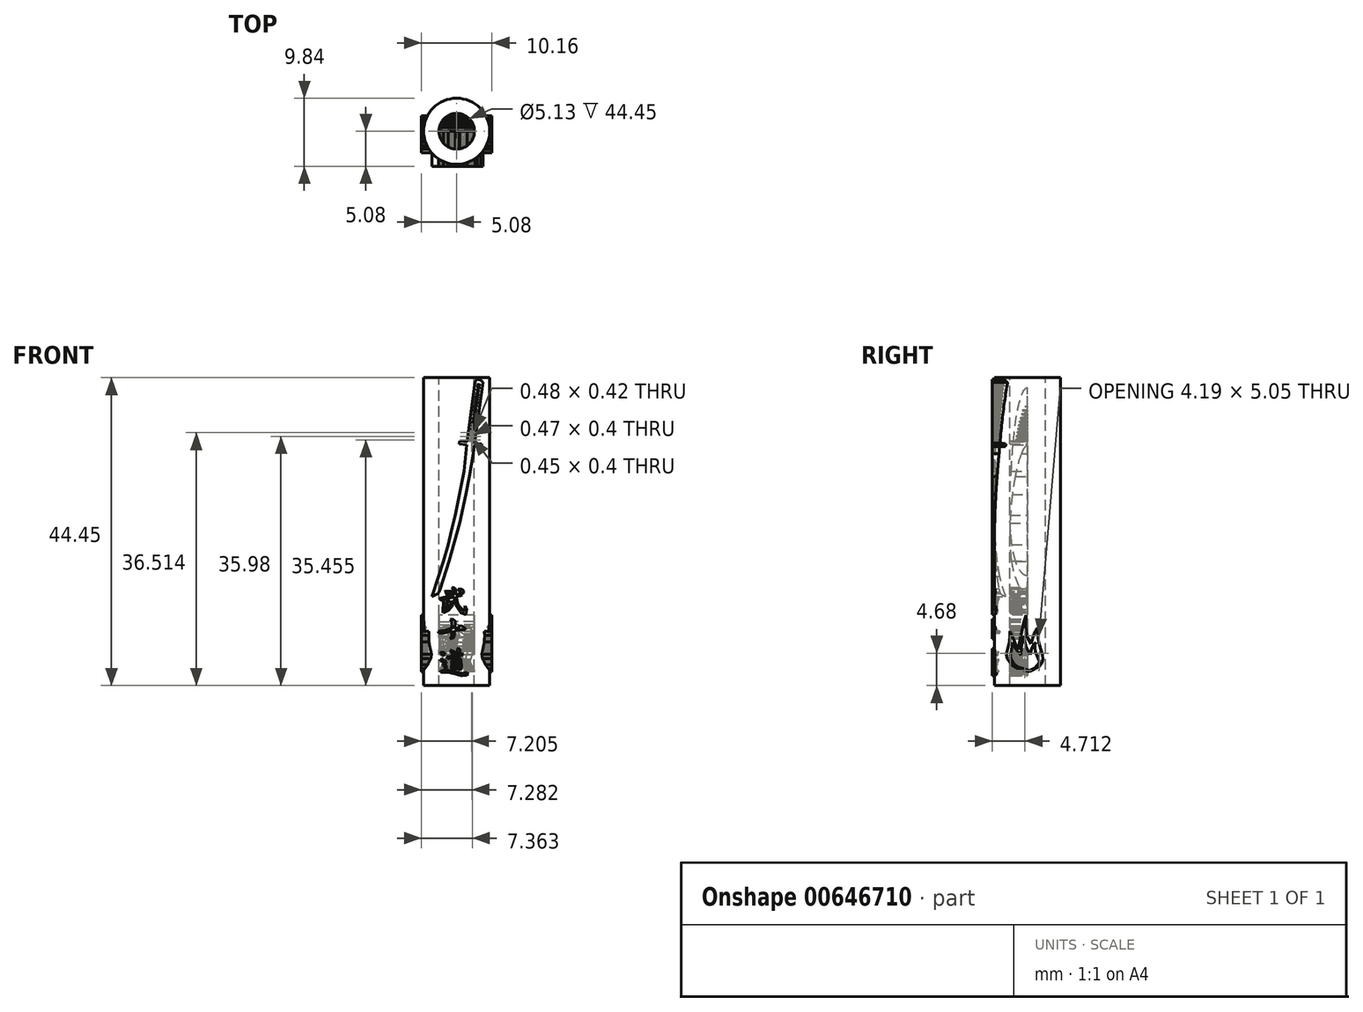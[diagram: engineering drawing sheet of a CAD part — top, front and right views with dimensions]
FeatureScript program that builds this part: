
annotation { "Feature Type Name" : "Feature", "Feature Type Description" : "" }
export const myFeature = defineFeature(function(context is Context, id is Id, definition is map)
    precondition{}
    {
        {
            var Q0;
            Q0=qCreatedBy(makeId("Top.planeOp"),FACE);
            var sketch = newSketch(context, id + "F0", { "sketchPlane" : qUnion([Q0])});
            skCircle(sketch, "E0", {"center": v(0, 0) * mm, "radius": 4.76 * mm});
            skSolve(sketch);
        }
        {
            var Q0;
            Q0=makeQuery(id+"F0.imprint","IMPRINT",FACE,{"disambiguationData":[TD([[makeQuery(id+"F0.imprint","IMPRINT",EDGE,{"derivedFrom":sQuery(id+"F0.wireOp",EDGE,"E0")}),1.0]])]});
            extrude(context, id + "F1", {"entities" : qUnion([Q0]), "depth" : 44.45 * mm, "offsetDistance" : 25.4 * mm});
        }
        {
            var Q0;
            Q0=makeQuery(id+"F1.opExtrude","CAP_FACE",FACE,{"disambiguationData":[OSD([sQuery(id+"F0.wireOp",EDGE,"E0")])],"isStart":false});
            var sketch = newSketch(context, id + "F2", { "sketchPlane" : qUnion([Q0])});
            skCircle(sketch, "E1", {"center": v(0, 0) * mm, "radius": 2.57 * mm});
            skSolve(sketch);
        }
        {
            var Q0;
            Q0=makeQuery(id+"F2.imprint","IMPRINT",FACE,{"disambiguationData":[TD([[makeQuery(id+"F2.imprint","IMPRINT",EDGE,{"derivedFrom":sQuery(id+"F2.wireOp",EDGE,"E1")}),1.0]])]});
            extrude(context, id + "F3", {"entities" : qUnion([Q0]), "operationType" : NewBodyOperationType.REMOVE, "oppositeDirection" : true, "depth" : 1270 * mm, "offsetDistance" : 25.4 * mm});
        }
        {
            var Q0;
            Q0=qCreatedBy(makeId("Front.planeOp"),FACE);
            var sketch = newSketch(context, id + "F4", { "sketchPlane" : qUnion([Q0])});
            skFitSpline(sketch, "E2", {"points": [v(-1.72, 13.56) * mm, v(-0.7, 13.54) * mm, v(-1.49, 13.18) * mm, v(-1.3, 13.33) * mm, v(-1.72, 13.56) * mm]});
            skFitSpline(sketch, "E3", {"points": [v(0.25, 13.88) * mm, v(0.93, 13.33) * mm, v(0.94, 13.74) * mm, v(0.25, 13.88) * mm]});
            skLineSegment(sketch, "E4", {"start": v(-0.68, 14.21) * mm, "end": v(-0.36, 14.14) * mm});
            skLineSegment(sketch, "E5", {"start": v(-0.36, 14.14) * mm, "end": v(-0.16, 13.94) * mm});
            skLineSegment(sketch, "E6", {"start": v(-0.16, 13.94) * mm, "end": v(-0.16, 13.14) * mm});
            skLineSegment(sketch, "E7", {"start": v(-0.16, 13.14) * mm, "end": v(0.61, 13.28) * mm});
            skLineSegment(sketch, "E8", {"start": v(0.61, 13.28) * mm, "end": v(0.83, 13.1) * mm});
            skLineSegment(sketch, "E9", {"start": v(0.83, 13.1) * mm, "end": v(0.56, 12.96) * mm});
            skLineSegment(sketch, "E10", {"start": v(0.56, 12.96) * mm, "end": v(-0.06, 12.84) * mm});
            skLineSegment(sketch, "E11", {"start": v(-0.06, 12.84) * mm, "end": v(0.15, 11.71) * mm});
            skLineSegment(sketch, "E12", {"start": v(0.15, 11.71) * mm, "end": v(1.06, 10.66) * mm});
            skLineSegment(sketch, "E13", {"start": v(1.06, 10.66) * mm, "end": v(1.21, 11.07) * mm});
            skLineSegment(sketch, "E14", {"start": v(1.21, 11.07) * mm, "end": v(1.21, 11.51) * mm});
            skLineSegment(sketch, "E15", {"start": v(1.21, 11.51) * mm, "end": v(1.43, 11.02) * mm});
            skLineSegment(sketch, "E16", {"start": v(1.43, 11.02) * mm, "end": v(1.34, 10.24) * mm});
            skLineSegment(sketch, "E17", {"start": v(1.34, 10.24) * mm, "end": v(0.65, 10.51) * mm});
            skLineSegment(sketch, "E18", {"start": v(0.65, 10.51) * mm, "end": v(-0.11, 11.63) * mm});
            skLineSegment(sketch, "E19", {"start": v(-0.11, 11.63) * mm, "end": v(-0.4, 12.8) * mm});
            skLineSegment(sketch, "E20", {"start": v(-0.4, 12.8) * mm, "end": v(-1.27, 12.58) * mm});
            skLineSegment(sketch, "E21", {"start": v(-1.27, 12.58) * mm, "end": v(-1.2, 12.32) * mm});
            skLineSegment(sketch, "E22", {"start": v(-1.2, 12.32) * mm, "end": v(-1.03, 12.15) * mm});
            skLineSegment(sketch, "E23", {"start": v(-1.03, 12.15) * mm, "end": v(-1.03, 11.99) * mm});
            skLineSegment(sketch, "E24", {"start": v(-1.03, 11.99) * mm, "end": v(-0.71, 12.08) * mm});
            skLineSegment(sketch, "E25", {"start": v(-0.71, 12.08) * mm, "end": v(-0.47, 12.08) * mm});
            skLineSegment(sketch, "E26", {"start": v(-0.47, 12.08) * mm, "end": v(-0.63, 11.8) * mm});
            skLineSegment(sketch, "E27", {"start": v(-0.63, 11.8) * mm, "end": v(-1.05, 11.8) * mm});
            skLineSegment(sketch, "E28", {"start": v(-1.05, 11.8) * mm, "end": v(-1.15, 11.27) * mm});
            skLineSegment(sketch, "E29", {"start": v(-1.15, 11.27) * mm, "end": v(-0.79, 11.44) * mm});
            skLineSegment(sketch, "E30", {"start": v(-0.79, 11.44) * mm, "end": v(-0.51, 11.67) * mm});
            skLineSegment(sketch, "E31", {"start": v(-0.51, 11.67) * mm, "end": v(-1.15, 10.88) * mm});
            skLineSegment(sketch, "E32", {"start": v(-1.15, 10.88) * mm, "end": v(-1.9, 10.51) * mm});
            skLineSegment(sketch, "E33", {"start": v(-1.9, 10.51) * mm, "end": v(-2, 10.7) * mm});
            skLineSegment(sketch, "E34", {"start": v(-2, 10.7) * mm, "end": v(-2, 11.03) * mm});
            skLineSegment(sketch, "E35", {"start": v(-2, 11.03) * mm, "end": v(-1.92, 11.92) * mm});
            skLineSegment(sketch, "E36", {"start": v(-1.92, 11.92) * mm, "end": v(-1.92, 12.17) * mm});
            skLineSegment(sketch, "E37", {"start": v(-1.92, 12.17) * mm, "end": v(-1.74, 11.96) * mm});
            skLineSegment(sketch, "E38", {"start": v(-1.74, 11.96) * mm, "end": v(-1.68, 11.7) * mm});
            skLineSegment(sketch, "E39", {"start": v(-1.68, 11.7) * mm, "end": v(-1.82, 10.9) * mm});
            skLineSegment(sketch, "E40", {"start": v(-1.82, 10.9) * mm, "end": v(-1.36, 11.09) * mm});
            skLineSegment(sketch, "E41", {"start": v(-1.36, 11.09) * mm, "end": v(-1.36, 11.97) * mm});
            skLineSegment(sketch, "E42", {"start": v(-1.36, 11.97) * mm, "end": v(-1.44, 12.52) * mm});
            skLineSegment(sketch, "E43", {"start": v(-1.44, 12.52) * mm, "end": v(-1.92, 12.32) * mm});
            skLineSegment(sketch, "E44", {"start": v(-1.92, 12.32) * mm, "end": v(-2.28, 12.32) * mm});
            skLineSegment(sketch, "E45", {"start": v(-2.28, 12.32) * mm, "end": v(-2.5, 12.57) * mm});
            skLineSegment(sketch, "E46", {"start": v(-2.5, 12.57) * mm, "end": v(-2.15, 12.65) * mm});
            skLineSegment(sketch, "E47", {"start": v(-2.15, 12.65) * mm, "end": v(-0.41, 13.1) * mm});
            skLineSegment(sketch, "E48", {"start": v(-0.41, 13.1) * mm, "end": v(-0.51, 13.97) * mm});
            skLineSegment(sketch, "E49", {"start": v(-0.51, 13.97) * mm, "end": v(-0.68, 14.21) * mm});
            skLineSegment(sketch, "E50", {"start": v(-0.89, 9.55) * mm, "end": v(-0.68, 9.62) * mm});
            skLineSegment(sketch, "E51", {"start": v(-0.68, 9.62) * mm, "end": v(-0.51, 9.55) * mm});
            skLineSegment(sketch, "E52", {"start": v(-0.51, 9.55) * mm, "end": v(-0.23, 9.3) * mm});
            skLineSegment(sketch, "E53", {"start": v(-0.23, 9.3) * mm, "end": v(-0.3, 8.3) * mm});
            skLineSegment(sketch, "E54", {"start": v(-0.3, 8.3) * mm, "end": v(0.5, 8.42) * mm});
            skLineSegment(sketch, "E55", {"start": v(0.5, 8.42) * mm, "end": v(0.41, 8.46) * mm});
            skLineSegment(sketch, "E56", {"start": v(0.41, 8.46) * mm, "end": v(0.25, 8.65) * mm});
            skLineSegment(sketch, "E57", {"start": v(0.25, 8.65) * mm, "end": v(0.81, 8.58) * mm});
            skLineSegment(sketch, "E58", {"start": v(0.81, 8.58) * mm, "end": v(1.24, 8.2) * mm});
            skLineSegment(sketch, "E59", {"start": v(1.24, 8.2) * mm, "end": v(1.24, 8.09) * mm});
            skLineSegment(sketch, "E60", {"start": v(1.24, 8.09) * mm, "end": v(-0.29, 8) * mm});
            skLineSegment(sketch, "E61", {"start": v(-0.29, 8) * mm, "end": v(-0.36, 6.97) * mm});
            skLineSegment(sketch, "E62", {"start": v(-0.36, 6.97) * mm, "end": v(-0.55, 6.86) * mm});
            skLineSegment(sketch, "E63", {"start": v(-0.55, 6.86) * mm, "end": v(-0.95, 6.74) * mm});
            skLineSegment(sketch, "E64", {"start": v(-0.95, 6.74) * mm, "end": v(-0.75, 6.96) * mm});
            skLineSegment(sketch, "E65", {"start": v(-0.75, 6.96) * mm, "end": v(-0.69, 7.43) * mm});
            skLineSegment(sketch, "E66", {"start": v(-0.69, 7.43) * mm, "end": v(-0.69, 7.92) * mm});
            skLineSegment(sketch, "E67", {"start": v(-0.69, 7.92) * mm, "end": v(-1.85, 7.55) * mm});
            skLineSegment(sketch, "E68", {"start": v(-1.85, 7.55) * mm, "end": v(-2.27, 7.55) * mm});
            skLineSegment(sketch, "E69", {"start": v(-2.27, 7.55) * mm, "end": v(-2.56, 7.59) * mm});
            skLineSegment(sketch, "E70", {"start": v(-2.56, 7.59) * mm, "end": v(-2.68, 7.83) * mm});
            skLineSegment(sketch, "E71", {"start": v(-2.68, 7.83) * mm, "end": v(-1.76, 7.93) * mm});
            skLineSegment(sketch, "E72", {"start": v(-1.76, 7.93) * mm, "end": v(-0.68, 8.26) * mm});
            skLineSegment(sketch, "E73", {"start": v(-0.68, 8.26) * mm, "end": v(-0.68, 9.2) * mm});
            skLineSegment(sketch, "E74", {"start": v(-0.68, 9.2) * mm, "end": v(-0.89, 9.55) * mm});
            skLineSegment(sketch, "E75", {"start": v(-1.8, 6.57) * mm, "end": v(-0.72, 6.7) * mm});
            skLineSegment(sketch, "E76", {"start": v(-0.72, 6.7) * mm, "end": v(-0.1, 6.8) * mm});
            skLineSegment(sketch, "E77", {"start": v(-0.1, 6.8) * mm, "end": v(0.18, 6.87) * mm});
            skLineSegment(sketch, "E78", {"start": v(0.18, 6.87) * mm, "end": v(0.36, 6.86) * mm});
            skLineSegment(sketch, "E79", {"start": v(0.36, 6.86) * mm, "end": v(0.6, 6.77) * mm});
            skLineSegment(sketch, "E80", {"start": v(0.6, 6.77) * mm, "end": v(0.7, 6.52) * mm});
            skLineSegment(sketch, "E81", {"start": v(0.7, 6.52) * mm, "end": v(0.41, 6.52) * mm});
            skLineSegment(sketch, "E82", {"start": v(0.41, 6.52) * mm, "end": v(0, 6.52) * mm});
            skLineSegment(sketch, "E83", {"start": v(0, 6.52) * mm, "end": v(-0.44, 6.52) * mm});
            skLineSegment(sketch, "E84", {"start": v(-0.44, 6.52) * mm, "end": v(-1.08, 6.37) * mm});
            skLineSegment(sketch, "E85", {"start": v(-1.08, 6.37) * mm, "end": v(-1.48, 6.3) * mm});
            skLineSegment(sketch, "E86", {"start": v(-1.48, 6.3) * mm, "end": v(-1.63, 6.37) * mm});
            skLineSegment(sketch, "E87", {"start": v(-1.63, 6.37) * mm, "end": v(-1.8, 6.56) * mm});
            skLineSegment(sketch, "E88", {"start": v(-2.31, 4.85) * mm, "end": v(-1.9, 4.8) * mm});
            skLineSegment(sketch, "E89", {"start": v(-1.9, 4.8) * mm, "end": v(-1.75, 4.72) * mm});
            skLineSegment(sketch, "E90", {"start": v(-1.75, 4.72) * mm, "end": v(-1.7, 4.52) * mm});
            skLineSegment(sketch, "E91", {"start": v(-1.7, 4.52) * mm, "end": v(-2.05, 4.37) * mm});
            skLineSegment(sketch, "E92", {"start": v(-2.05, 4.37) * mm, "end": v(-2.07, 4.47) * mm});
            skLineSegment(sketch, "E93", {"start": v(-2.07, 4.47) * mm, "end": v(-1.98, 4.49) * mm});
            skLineSegment(sketch, "E94", {"start": v(-1.98, 4.49) * mm, "end": v(-2.27, 4.65) * mm});
            skLineSegment(sketch, "E95", {"start": v(-2.27, 4.65) * mm, "end": v(-2.31, 4.85) * mm});
            skLineSegment(sketch, "E96", {"start": v(-0.68, 5.18) * mm, "end": v(-0.65, 5.05) * mm});
            skLineSegment(sketch, "E97", {"start": v(-0.65, 5.05) * mm, "end": v(-0.51, 4.88) * mm});
            skLineSegment(sketch, "E98", {"start": v(-0.51, 4.88) * mm, "end": v(-0.26, 5.04) * mm});
            skLineSegment(sketch, "E99", {"start": v(-0.26, 5.04) * mm, "end": v(-0.46, 4.54) * mm});
            skLineSegment(sketch, "E100", {"start": v(-0.46, 4.54) * mm, "end": v(-0.72, 4.7) * mm});
            skLineSegment(sketch, "E101", {"start": v(-0.72, 4.7) * mm, "end": v(-0.83, 4.91) * mm});
            skLineSegment(sketch, "E102", {"start": v(-0.83, 4.91) * mm, "end": v(-0.83, 5.09) * mm});
            skLineSegment(sketch, "E103", {"start": v(-0.83, 5.09) * mm, "end": v(-0.68, 5.18) * mm});
            skLineSegment(sketch, "E104", {"start": v(0.15, 5.33) * mm, "end": v(0.36, 5.3) * mm});
            skLineSegment(sketch, "E105", {"start": v(0.36, 5.3) * mm, "end": v(0.49, 5.1) * mm});
            skLineSegment(sketch, "E106", {"start": v(0.49, 5.1) * mm, "end": v(0.52, 4.99) * mm});
            skLineSegment(sketch, "E107", {"start": v(0.52, 4.99) * mm, "end": v(0.03, 4.61) * mm});
            skLineSegment(sketch, "E108", {"start": v(0.03, 4.61) * mm, "end": v(-0.37, 4.44) * mm});
            skLineSegment(sketch, "E109", {"start": v(-0.37, 4.44) * mm, "end": v(-0.2, 4.41) * mm});
            skLineSegment(sketch, "E110", {"start": v(-0.2, 4.41) * mm, "end": v(0.3, 4.59) * mm});
            skLineSegment(sketch, "E111", {"start": v(0.3, 4.59) * mm, "end": v(0.66, 4.63) * mm});
            skLineSegment(sketch, "E112", {"start": v(0.66, 4.63) * mm, "end": v(0.8, 4.57) * mm});
            skLineSegment(sketch, "E113", {"start": v(0.8, 4.57) * mm, "end": v(0.96, 4.41) * mm});
            skLineSegment(sketch, "E114", {"start": v(0.96, 4.41) * mm, "end": v(-0.2, 4.25) * mm});
            skLineSegment(sketch, "E115", {"start": v(-0.2, 4.25) * mm, "end": v(-0.22, 3.94) * mm});
            skLineSegment(sketch, "E116", {"start": v(-0.22, 3.94) * mm, "end": v(-0.27, 3.87) * mm});
            skLineSegment(sketch, "E117", {"start": v(-0.27, 3.87) * mm, "end": v(0.06, 3.97) * mm});
            skLineSegment(sketch, "E118", {"start": v(0.06, 3.97) * mm, "end": v(0.43, 4.02) * mm});
            skLineSegment(sketch, "E119", {"start": v(0.43, 4.02) * mm, "end": v(0.63, 3.8) * mm});
            skLineSegment(sketch, "E120", {"start": v(0.63, 3.8) * mm, "end": v(0.67, 2.66) * mm});
            skLineSegment(sketch, "E121", {"start": v(0.67, 2.66) * mm, "end": v(0.65, 2.5) * mm});
            skLineSegment(sketch, "E122", {"start": v(0.65, 2.5) * mm, "end": v(0.52, 2.17) * mm});
            skLineSegment(sketch, "E123", {"start": v(0.52, 2.17) * mm, "end": v(0.36, 2.37) * mm});
            skLineSegment(sketch, "E124", {"start": v(0.36, 2.37) * mm, "end": v(0.36, 3.32) * mm});
            skLineSegment(sketch, "E125", {"start": v(0.36, 3.32) * mm, "end": v(0.36, 3.56) * mm});
            skLineSegment(sketch, "E126", {"start": v(0.36, 3.56) * mm, "end": v(0.28, 3.78) * mm});
            skLineSegment(sketch, "E127", {"start": v(0.28, 3.78) * mm, "end": v(0.06, 3.73) * mm});
            skLineSegment(sketch, "E128", {"start": v(0.06, 3.73) * mm, "end": v(-0.24, 3.76) * mm});
            skLineSegment(sketch, "E129", {"start": v(-0.24, 3.76) * mm, "end": v(-0.43, 3.76) * mm});
            skLineSegment(sketch, "E130", {"start": v(-0.43, 3.76) * mm, "end": v(-0.56, 3.68) * mm});
            skLineSegment(sketch, "E131", {"start": v(-0.56, 3.68) * mm, "end": v(-0.51, 3.5) * mm});
            skLineSegment(sketch, "E132", {"start": v(-0.51, 3.5) * mm, "end": v(-0.5, 3.46) * mm});
            skLineSegment(sketch, "E133", {"start": v(-0.5, 3.46) * mm, "end": v(-0.24, 3.5) * mm});
            skLineSegment(sketch, "E134", {"start": v(-0.24, 3.5) * mm, "end": v(-0.02, 3.55) * mm});
            skLineSegment(sketch, "E135", {"start": v(-0.02, 3.55) * mm, "end": v(0.1, 3.54) * mm});
            skLineSegment(sketch, "E136", {"start": v(0.1, 3.54) * mm, "end": v(0.19, 3.46) * mm});
            skLineSegment(sketch, "E137", {"start": v(0.19, 3.46) * mm, "end": v(0.08, 3.36) * mm});
            skLineSegment(sketch, "E138", {"start": v(0.08, 3.36) * mm, "end": v(-0.17, 3.27) * mm});
            skLineSegment(sketch, "E139", {"start": v(-0.17, 3.27) * mm, "end": v(-0.3, 3.18) * mm});
            skLineSegment(sketch, "E140", {"start": v(-0.3, 3.18) * mm, "end": v(-0.32, 3.2) * mm});
            skLineSegment(sketch, "E141", {"start": v(-0.32, 3.2) * mm, "end": v(-0.24, 3.28) * mm});
            skLineSegment(sketch, "E142", {"start": v(-0.24, 3.28) * mm, "end": v(-0.29, 3.3) * mm});
            skLineSegment(sketch, "E143", {"start": v(-0.29, 3.3) * mm, "end": v(-0.53, 3.3) * mm});
            skLineSegment(sketch, "E144", {"start": v(-0.53, 3.3) * mm, "end": v(-0.53, 3.07) * mm});
            skLineSegment(sketch, "E145", {"start": v(-0.53, 3.07) * mm, "end": v(-0.33, 3.07) * mm});
            skLineSegment(sketch, "E146", {"start": v(-0.33, 3.07) * mm, "end": v(-0.01, 3.14) * mm});
            skLineSegment(sketch, "E147", {"start": v(-0.01, 3.14) * mm, "end": v(0.15, 3.14) * mm});
            skLineSegment(sketch, "E148", {"start": v(0.15, 3.14) * mm, "end": v(0.24, 3.07) * mm});
            skLineSegment(sketch, "E149", {"start": v(0.24, 3.07) * mm, "end": v(0.2, 2.97) * mm});
            skLineSegment(sketch, "E150", {"start": v(0.2, 2.97) * mm, "end": v(-0.04, 2.85) * mm});
            skLineSegment(sketch, "E151", {"start": v(-0.04, 2.85) * mm, "end": v(-0.2, 2.74) * mm});
            skLineSegment(sketch, "E152", {"start": v(-0.2, 2.74) * mm, "end": v(-0.23, 2.77) * mm});
            skLineSegment(sketch, "E153", {"start": v(-0.23, 2.77) * mm, "end": v(-0.09, 2.9) * mm});
            skLineSegment(sketch, "E154", {"start": v(-0.09, 2.9) * mm, "end": v(-0.5, 2.94) * mm});
            skLineSegment(sketch, "E155", {"start": v(-0.5, 2.94) * mm, "end": v(-0.54, 2.86) * mm});
            skLineSegment(sketch, "E156", {"start": v(-0.54, 2.86) * mm, "end": v(-0.55, 2.59) * mm});
            skLineSegment(sketch, "E157", {"start": v(-0.55, 2.59) * mm, "end": v(-0.42, 2.64) * mm});
            skLineSegment(sketch, "E158", {"start": v(-0.42, 2.64) * mm, "end": v(-0.43, 2.61) * mm});
            skLineSegment(sketch, "E159", {"start": v(-0.43, 2.61) * mm, "end": v(-0.24, 2.59) * mm});
            skLineSegment(sketch, "E160", {"start": v(-0.24, 2.59) * mm, "end": v(0.06, 2.66) * mm});
            skLineSegment(sketch, "E161", {"start": v(0.06, 2.66) * mm, "end": v(0.23, 2.63) * mm});
            skLineSegment(sketch, "E162", {"start": v(0.23, 2.63) * mm, "end": v(0.3, 2.5) * mm});
            skLineSegment(sketch, "E163", {"start": v(0.3, 2.5) * mm, "end": v(0.28, 2.46) * mm});
            skLineSegment(sketch, "E164", {"start": v(0.28, 2.46) * mm, "end": v(0.1, 2.42) * mm});
            skLineSegment(sketch, "E165", {"start": v(0.1, 2.42) * mm, "end": v(-0.24, 2.42) * mm});
            skLineSegment(sketch, "E166", {"start": v(-0.24, 2.42) * mm, "end": v(-0.5, 2.39) * mm});
            skLineSegment(sketch, "E167", {"start": v(-0.5, 2.39) * mm, "end": v(-0.66, 2.29) * mm});
            skLineSegment(sketch, "E168", {"start": v(-0.66, 2.29) * mm, "end": v(-0.77, 2.62) * mm});
            skLineSegment(sketch, "E169", {"start": v(-0.77, 2.62) * mm, "end": v(-0.73, 3.12) * mm});
            skLineSegment(sketch, "E170", {"start": v(-0.73, 3.12) * mm, "end": v(-0.68, 3.48) * mm});
            skLineSegment(sketch, "E171", {"start": v(-0.68, 3.48) * mm, "end": v(-0.75, 3.67) * mm});
            skLineSegment(sketch, "E172", {"start": v(-0.75, 3.67) * mm, "end": v(-0.38, 4.17) * mm});
            skLineSegment(sketch, "E173", {"start": v(-0.38, 4.17) * mm, "end": v(-1.14, 3.88) * mm});
            skLineSegment(sketch, "E174", {"start": v(-1.14, 3.88) * mm, "end": v(-1.32, 3.9) * mm});
            skLineSegment(sketch, "E175", {"start": v(-1.32, 3.9) * mm, "end": v(-1.43, 4.02) * mm});
            skLineSegment(sketch, "E176", {"start": v(-1.43, 4.02) * mm, "end": v(-1.44, 4.14) * mm});
            skLineSegment(sketch, "E177", {"start": v(-1.44, 4.14) * mm, "end": v(-1.18, 4.14) * mm});
            skLineSegment(sketch, "E178", {"start": v(-1.18, 4.14) * mm, "end": v(-0.71, 4.28) * mm});
            skLineSegment(sketch, "E179", {"start": v(-0.71, 4.28) * mm, "end": v(-0.23, 4.62) * mm});
            skLineSegment(sketch, "E180", {"start": v(-0.23, 4.62) * mm, "end": v(0.18, 5.06) * mm});
            skLineSegment(sketch, "E181", {"start": v(0.18, 5.06) * mm, "end": v(0.14, 5.2) * mm});
            skLineSegment(sketch, "E182", {"start": v(0.14, 5.2) * mm, "end": v(0.12, 5.3) * mm});
            skLineSegment(sketch, "E183", {"start": v(0.12, 5.3) * mm, "end": v(0.15, 5.34) * mm});
            skLineSegment(sketch, "E184", {"start": v(0.15, 5.34) * mm, "end": v(0.15, 5.33) * mm});
            skLineSegment(sketch, "E185", {"start": v(-2.34, 3.75) * mm, "end": v(-2.13, 3.77) * mm});
            skLineSegment(sketch, "E186", {"start": v(-2.13, 3.77) * mm, "end": v(-1.9, 3.74) * mm});
            skLineSegment(sketch, "E187", {"start": v(-1.9, 3.74) * mm, "end": v(-1.66, 3.6) * mm});
            skLineSegment(sketch, "E188", {"start": v(-1.66, 3.6) * mm, "end": v(-1.56, 3.43) * mm});
            skLineSegment(sketch, "E189", {"start": v(-1.56, 3.43) * mm, "end": v(-1.56, 3.23) * mm});
            skLineSegment(sketch, "E190", {"start": v(-1.56, 3.23) * mm, "end": v(-1.68, 3.03) * mm});
            skLineSegment(sketch, "E191", {"start": v(-1.68, 3.03) * mm, "end": v(-1.46, 2.69) * mm});
            skLineSegment(sketch, "E192", {"start": v(-1.46, 2.69) * mm, "end": v(-1.41, 2.48) * mm});
            skLineSegment(sketch, "E193", {"start": v(-1.41, 2.48) * mm, "end": v(-1.46, 2.28) * mm});
            skLineSegment(sketch, "E194", {"start": v(-1.46, 2.28) * mm, "end": v(-1.6, 2.17) * mm});
            skLineSegment(sketch, "E195", {"start": v(-1.6, 2.17) * mm, "end": v(-1.15, 2.17) * mm});
            skLineSegment(sketch, "E196", {"start": v(-1.15, 2.17) * mm, "end": v(-0.48, 2.05) * mm});
            skLineSegment(sketch, "E197", {"start": v(-0.48, 2.05) * mm, "end": v(0.24, 1.87) * mm});
            skLineSegment(sketch, "E198", {"start": v(0.24, 1.87) * mm, "end": v(0.77, 1.77) * mm});
            skLineSegment(sketch, "E199", {"start": v(0.77, 1.77) * mm, "end": v(1.26, 1.85) * mm});
            skLineSegment(sketch, "E200", {"start": v(1.26, 1.85) * mm, "end": v(1.47, 1.85) * mm});
            skLineSegment(sketch, "E201", {"start": v(1.47, 1.85) * mm, "end": v(1.68, 1.7) * mm});
            skLineSegment(sketch, "E202", {"start": v(1.68, 1.7) * mm, "end": v(1.33, 1.51) * mm});
            skLineSegment(sketch, "E203", {"start": v(1.33, 1.51) * mm, "end": v(0.78, 1.45) * mm});
            skLineSegment(sketch, "E204", {"start": v(0.78, 1.45) * mm, "end": v(0.26, 1.57) * mm});
            skLineSegment(sketch, "E205", {"start": v(0.26, 1.57) * mm, "end": v(-0.6, 1.8) * mm});
            skLineSegment(sketch, "E206", {"start": v(-0.6, 1.8) * mm, "end": v(-1.2, 1.93) * mm});
            skLineSegment(sketch, "E207", {"start": v(-1.2, 1.93) * mm, "end": v(-2, 1.9) * mm});
            skLineSegment(sketch, "E208", {"start": v(-2, 1.9) * mm, "end": v(-2.14, 1.9) * mm});
            skLineSegment(sketch, "E209", {"start": v(-2.14, 1.9) * mm, "end": v(-2.29, 2) * mm});
            skLineSegment(sketch, "E210", {"start": v(-2.29, 2) * mm, "end": v(-2.29, 2.17) * mm});
            skLineSegment(sketch, "E211", {"start": v(-2.29, 2.17) * mm, "end": v(-2.08, 2.14) * mm});
            skLineSegment(sketch, "E212", {"start": v(-2.08, 2.14) * mm, "end": v(-1.84, 2.19) * mm});
            skLineSegment(sketch, "E213", {"start": v(-1.84, 2.19) * mm, "end": v(-1.68, 2.4) * mm});
            skLineSegment(sketch, "E214", {"start": v(-1.68, 2.4) * mm, "end": v(-1.68, 2.62) * mm});
            skLineSegment(sketch, "E215", {"start": v(-1.68, 2.62) * mm, "end": v(-1.9, 2.94) * mm});
            skLineSegment(sketch, "E216", {"start": v(-1.9, 2.94) * mm, "end": v(-1.96, 3.22) * mm});
            skLineSegment(sketch, "E217", {"start": v(-1.96, 3.22) * mm, "end": v(-1.87, 3.43) * mm});
            skLineSegment(sketch, "E218", {"start": v(-1.87, 3.43) * mm, "end": v(-1.98, 3.44) * mm});
            skLineSegment(sketch, "E219", {"start": v(-1.98, 3.44) * mm, "end": v(-2.15, 3.44) * mm});
            skLineSegment(sketch, "E220", {"start": v(-2.15, 3.44) * mm, "end": v(-2.29, 3.57) * mm});
            skLineSegment(sketch, "E221", {"start": v(-2.29, 3.57) * mm, "end": v(-2.34, 3.69) * mm});
            skLineSegment(sketch, "E222", {"start": v(-2.34, 3.69) * mm, "end": v(-2.34, 3.75) * mm});
            skSolve(sketch);
        }
        {
            var Q0;
            Q0 = qSketchRegion(id + "F4", true);
            extrude(context, id + "F5", {"entities" : qUnion([Q0]), "operationType" : NewBodyOperationType.ADD, "depth" : 5.08 * mm, "offsetDistance" : 25.4 * mm});
        }
        {
            var Q0;
            Q0=qCreatedBy(makeId("Front.planeOp"),FACE);
            var sketch = newSketch(context, id + "F6", { "sketchPlane" : qUnion([Q0])});
            skLineSegment(sketch, "E223", {"start": v(1.52, 35.18) * mm, "end": v(2.68, 43.9) * mm});
            skLineSegment(sketch, "E224", {"start": v(2.68, 43.9) * mm, "end": v(2.98, 44.2) * mm});
            skLineSegment(sketch, "E225", {"start": v(2.98, 44.2) * mm, "end": v(3.52, 44.12) * mm});
            skLineSegment(sketch, "E226", {"start": v(3.52, 44.12) * mm, "end": v(3.78, 43.76) * mm});
            skLineSegment(sketch, "E227", {"start": v(3.78, 43.76) * mm, "end": v(2.62, 35.03) * mm});
            skLineSegment(sketch, "E228", {"start": v(0.37, 34.9) * mm, "end": v(0.42, 35.32) * mm});
            skLineSegment(sketch, "E229", {"start": v(0.42, 35.32) * mm, "end": v(3.6, 34.9) * mm});
            skLineSegment(sketch, "E230", {"start": v(3.6, 34.9) * mm, "end": v(3.54, 34.49) * mm});
            skLineSegment(sketch, "E231", {"start": v(3.54, 34.49) * mm, "end": v(0.37, 34.9) * mm});
            skLineSegment(sketch, "E232", {"start": v(1.9, 35.49) * mm, "end": v(2.04, 35.26) * mm});
            skLineSegment(sketch, "E233", {"start": v(2.04, 35.26) * mm, "end": v(2.35, 35.45) * mm});
            skLineSegment(sketch, "E234", {"start": v(2.35, 35.45) * mm, "end": v(2.22, 35.65) * mm});
            skLineSegment(sketch, "E235", {"start": v(2.22, 35.65) * mm, "end": v(1.9, 35.49) * mm});
            skLineSegment(sketch, "E236", {"start": v(1.97, 36) * mm, "end": v(2.17, 35.78) * mm});
            skLineSegment(sketch, "E237", {"start": v(2.17, 35.78) * mm, "end": v(2.44, 36.01) * mm});
            skLineSegment(sketch, "E238", {"start": v(2.44, 36.01) * mm, "end": v(2.3, 36.18) * mm});
            skLineSegment(sketch, "E239", {"start": v(2.3, 36.18) * mm, "end": v(1.97, 36) * mm});
            skLineSegment(sketch, "E240", {"start": v(2.04, 36.56) * mm, "end": v(2.3, 36.3) * mm});
            skLineSegment(sketch, "E241", {"start": v(2.3, 36.3) * mm, "end": v(2.52, 36.53) * mm});
            skLineSegment(sketch, "E242", {"start": v(2.52, 36.53) * mm, "end": v(2.34, 36.73) * mm});
            skLineSegment(sketch, "E243", {"start": v(2.34, 36.73) * mm, "end": v(2.04, 36.56) * mm});
            skLineSegment(sketch, "E244", {"start": v(2.1, 37.07) * mm, "end": v(2.33, 36.87) * mm});
            skLineSegment(sketch, "E245", {"start": v(2.33, 36.87) * mm, "end": v(2.57, 36.99) * mm});
            skLineSegment(sketch, "E246", {"start": v(2.57, 36.99) * mm, "end": v(2.38, 37.19) * mm});
            skLineSegment(sketch, "E247", {"start": v(2.38, 37.19) * mm, "end": v(2.1, 37.07) * mm});
            skLineSegment(sketch, "E248", {"start": v(2.18, 37.6) * mm, "end": v(2.36, 37.37) * mm});
            skLineSegment(sketch, "E249", {"start": v(2.36, 37.37) * mm, "end": v(2.66, 37.52) * mm});
            skLineSegment(sketch, "E250", {"start": v(2.66, 37.52) * mm, "end": v(2.55, 37.75) * mm});
            skLineSegment(sketch, "E251", {"start": v(2.55, 37.75) * mm, "end": v(2.18, 37.6) * mm});
            skLineSegment(sketch, "E252", {"start": v(2.25, 38.11) * mm, "end": v(2.42, 37.88) * mm});
            skLineSegment(sketch, "E253", {"start": v(2.42, 37.88) * mm, "end": v(2.7, 38.09) * mm});
            skLineSegment(sketch, "E254", {"start": v(2.7, 38.09) * mm, "end": v(2.57, 38.28) * mm});
            skLineSegment(sketch, "E255", {"start": v(2.57, 38.28) * mm, "end": v(2.25, 38.11) * mm});
            skLineSegment(sketch, "E256", {"start": v(2.32, 38.63) * mm, "end": v(2.46, 38.41) * mm});
            skLineSegment(sketch, "E257", {"start": v(2.46, 38.41) * mm, "end": v(2.74, 38.6) * mm});
            skLineSegment(sketch, "E258", {"start": v(2.74, 38.6) * mm, "end": v(2.63, 38.77) * mm});
            skLineSegment(sketch, "E259", {"start": v(2.63, 38.77) * mm, "end": v(2.32, 38.63) * mm});
            skLineSegment(sketch, "E260", {"start": v(2.4, 39.2) * mm, "end": v(2.57, 38.96) * mm});
            skLineSegment(sketch, "E261", {"start": v(2.57, 38.96) * mm, "end": v(2.81, 39.14) * mm});
            skLineSegment(sketch, "E262", {"start": v(2.81, 39.14) * mm, "end": v(2.7, 39.32) * mm});
            skLineSegment(sketch, "E263", {"start": v(2.7, 39.32) * mm, "end": v(2.4, 39.2) * mm});
            skLineSegment(sketch, "E264", {"start": v(2.45, 39.74) * mm, "end": v(2.6, 39.5) * mm});
            skLineSegment(sketch, "E265", {"start": v(2.6, 39.5) * mm, "end": v(2.89, 39.69) * mm});
            skLineSegment(sketch, "E266", {"start": v(2.89, 39.69) * mm, "end": v(2.76, 39.89) * mm});
            skLineSegment(sketch, "E267", {"start": v(2.76, 39.89) * mm, "end": v(2.45, 39.74) * mm});
            skLineSegment(sketch, "E268", {"start": v(2.54, 40.3) * mm, "end": v(2.69, 40.03) * mm});
            skLineSegment(sketch, "E269", {"start": v(2.69, 40.03) * mm, "end": v(2.94, 40.17) * mm});
            skLineSegment(sketch, "E270", {"start": v(2.94, 40.17) * mm, "end": v(2.82, 40.38) * mm});
            skLineSegment(sketch, "E271", {"start": v(2.82, 40.38) * mm, "end": v(2.54, 40.3) * mm});
            skLineSegment(sketch, "E272", {"start": v(2.6, 40.78) * mm, "end": v(2.78, 40.52) * mm});
            skLineSegment(sketch, "E273", {"start": v(2.78, 40.52) * mm, "end": v(3.07, 40.63) * mm});
            skLineSegment(sketch, "E274", {"start": v(3.07, 40.63) * mm, "end": v(2.96, 40.92) * mm});
            skLineSegment(sketch, "E275", {"start": v(2.96, 40.92) * mm, "end": v(2.6, 40.78) * mm});
            skLineSegment(sketch, "E276", {"start": v(2.67, 41.3) * mm, "end": v(2.83, 41.02) * mm});
            skLineSegment(sketch, "E277", {"start": v(2.83, 41.02) * mm, "end": v(3.09, 41.17) * mm});
            skLineSegment(sketch, "E278", {"start": v(3.09, 41.17) * mm, "end": v(2.96, 41.4) * mm});
            skLineSegment(sketch, "E279", {"start": v(2.96, 41.4) * mm, "end": v(2.67, 41.3) * mm});
            skLineSegment(sketch, "E280", {"start": v(2.74, 41.85) * mm, "end": v(2.92, 41.58) * mm});
            skLineSegment(sketch, "E281", {"start": v(2.92, 41.58) * mm, "end": v(3.2, 41.75) * mm});
            skLineSegment(sketch, "E282", {"start": v(3.2, 41.75) * mm, "end": v(3.05, 41.98) * mm});
            skLineSegment(sketch, "E283", {"start": v(3.05, 41.98) * mm, "end": v(2.74, 41.85) * mm});
            skLineSegment(sketch, "E284", {"start": v(2.82, 42.4) * mm, "end": v(2.93, 42.12) * mm});
            skLineSegment(sketch, "E285", {"start": v(2.93, 42.12) * mm, "end": v(3.22, 42.24) * mm});
            skLineSegment(sketch, "E286", {"start": v(3.22, 42.24) * mm, "end": v(3.13, 42.47) * mm});
            skLineSegment(sketch, "E287", {"start": v(3.13, 42.47) * mm, "end": v(2.82, 42.4) * mm});
            skLineSegment(sketch, "E288", {"start": v(2.89, 42.9) * mm, "end": v(3, 42.63) * mm});
            skLineSegment(sketch, "E289", {"start": v(3, 42.63) * mm, "end": v(3.3, 42.74) * mm});
            skLineSegment(sketch, "E290", {"start": v(3.3, 42.74) * mm, "end": v(3.2, 42.99) * mm});
            skLineSegment(sketch, "E291", {"start": v(3.2, 42.99) * mm, "end": v(2.89, 42.9) * mm});
            skPoint(sketch, "E292.orphan", {"position": v(2.89, 42.9) * mm});
            skLineSegment(sketch, "E293", {"start": v(2.93, 43.41) * mm, "end": v(3.07, 43.19) * mm});
            skPoint(sketch, "E293.endSnap0", {"position": v(2.97, 42.43) * mm});
            skLineSegment(sketch, "E294", {"start": v(3.07, 43.19) * mm, "end": v(3.4, 43.28) * mm});
            skLineSegment(sketch, "E295", {"start": v(3.4, 43.28) * mm, "end": v(3.24, 43.55) * mm});
            skLineSegment(sketch, "E296", {"start": v(3.24, 43.55) * mm, "end": v(2.93, 43.41) * mm});
            skLineSegment(sketch, "E297", {"start": v(1.46, 34.76) * mm, "end": v(1.8, 33.95) * mm});
            skLineSegment(sketch, "E298", {"start": v(1.8, 33.95) * mm, "end": v(2.56, 34.62) * mm});
            skLineSegment(sketch, "E299", {"start": v(2.56, 34.62) * mm, "end": v(2.4, 33.46) * mm});
            skLineSegment(sketch, "E300", {"start": v(2.4, 33.46) * mm, "end": v(1.85, 30.21) * mm});
            skLineSegment(sketch, "E301", {"start": v(1.85, 30.21) * mm, "end": v(1.33, 27.6) * mm});
            skLineSegment(sketch, "E302", {"start": v(1.33, 27.6) * mm, "end": v(0.42, 23.46) * mm});
            skLineSegment(sketch, "E303", {"start": v(0.42, 23.46) * mm, "end": v(-1.06, 17.97) * mm});
            skLineSegment(sketch, "E304", {"start": v(-1.06, 17.97) * mm, "end": v(-2.37, 14) * mm});
            skLineSegment(sketch, "E305", {"start": v(-2.37, 14) * mm, "end": v(-2.55, 13.5) * mm});
            skLineSegment(sketch, "E306", {"start": v(-2.55, 13.5) * mm, "end": v(-2.7, 13.29) * mm});
            skLineSegment(sketch, "E307", {"start": v(-2.7, 13.29) * mm, "end": v(-3.6, 12.87) * mm});
            skLineSegment(sketch, "E308", {"start": v(-3.6, 12.87) * mm, "end": v(-2.6, 15.75) * mm});
            skLineSegment(sketch, "E309", {"start": v(-2.6, 15.75) * mm, "end": v(-1.92, 17.9) * mm});
            skLineSegment(sketch, "E310", {"start": v(-1.92, 17.9) * mm, "end": v(-1.24, 20.35) * mm});
            skLineSegment(sketch, "E311", {"start": v(-1.24, 20.35) * mm, "end": v(-0.76, 22.3) * mm});
            skLineSegment(sketch, "E312", {"start": v(-0.76, 22.3) * mm, "end": v(-0.21, 24.6) * mm});
            skLineSegment(sketch, "E313", {"start": v(-0.21, 24.6) * mm, "end": v(0.18, 26.58) * mm});
            skLineSegment(sketch, "E314", {"start": v(0.18, 26.58) * mm, "end": v(0.66, 29.01) * mm});
            skLineSegment(sketch, "E315", {"start": v(0.66, 29.01) * mm, "end": v(1.04, 30.94) * mm});
            skLineSegment(sketch, "E316", {"start": v(1.04, 30.94) * mm, "end": v(1.46, 34.76) * mm});
            skLineSegment(sketch, "E317", {"start": v(1.8, 33.95) * mm, "end": v(1.3, 31.24) * mm});
            skLineSegment(sketch, "E318", {"start": v(1.3, 31.24) * mm, "end": v(0.7, 27.85) * mm});
            skLineSegment(sketch, "E319", {"start": v(0.7, 27.85) * mm, "end": v(0.43, 26.44) * mm});
            skLineSegment(sketch, "E320", {"start": v(0.43, 26.44) * mm, "end": v(0.09, 24.72) * mm});
            skLineSegment(sketch, "E321", {"start": v(0.09, 24.72) * mm, "end": v(-0.25, 23.32) * mm});
            skLineSegment(sketch, "E322", {"start": v(-0.25, 23.32) * mm, "end": v(-0.62, 21.84) * mm});
            skLineSegment(sketch, "E323", {"start": v(-0.62, 21.84) * mm, "end": v(-1.25, 19.32) * mm});
            skLineSegment(sketch, "E324", {"start": v(-1.25, 19.32) * mm, "end": v(-1.75, 17.49) * mm});
            skLineSegment(sketch, "E325", {"start": v(-1.75, 17.49) * mm, "end": v(-2.46, 15.27) * mm});
            skLineSegment(sketch, "E326", {"start": v(-2.46, 15.27) * mm, "end": v(-3, 13.77) * mm});
            skLineSegment(sketch, "E327", {"start": v(-3, 13.77) * mm, "end": v(-3.6, 12.87) * mm});
            skLineSegment(sketch, "E328.0", {"start": v(1.46, 34.76) * mm, "end": v(1.52, 35.18) * mm, "construction": true});
            skLineSegment(sketch, "E329.0", {"start": v(1.9, 35.49) * mm, "end": v(2.89, 42.9) * mm, "construction": true});
            skLineSegment(sketch, "E330.0", {"start": v(2.97, 42.43) * mm, "end": v(3.07, 43.19) * mm, "construction": true});
            skLineSegment(sketch, "E331.0", {"start": v(2.56, 34.62) * mm, "end": v(2.62, 35.03) * mm, "construction": true});
            skLineSegment(sketch, "E332.0", {"start": v(1.3, 31.24) * mm, "end": v(2.93, 43.41) * mm, "construction": true});
            skLineSegment(sketch, "E333.0", {"start": v(-0.25, 23.32) * mm, "end": v(0.18, 26.58) * mm, "construction": true});
            skLineSegment(sketch, "E334.0", {"start": v(1.52, 35.18) * mm, "end": v(0.42, 35.32) * mm, "construction": true});
            skLineSegment(sketch, "E335.0", {"start": v(3.54, 34.49) * mm, "end": v(0.37, 34.9) * mm, "construction": true});
            skSolve(sketch);
        }
        {
            var Q0;
            Q0 = qSketchRegion(id + "F6", true);
            extrude(context, id + "F7", {"entities" : qUnion([Q0]), "operationType" : NewBodyOperationType.ADD, "depth" : 5.08 * mm, "offsetDistance" : 25.4 * mm});
        }
        {
            var Q0;
            Q0=qCreatedBy(makeId("Right.planeOp"),FACE);
            var sketch = newSketch(context, id + "F8", { "sketchPlane" : qUnion([Q0])});
            skLineSegment(sketch, "E336", {"start": v(0.26, 12.17) * mm, "end": v(0, 11.12) * mm});
            skLineSegment(sketch, "E337", {"start": v(0, 11.12) * mm, "end": v(0.08, 10.02) * mm});
            skLineSegment(sketch, "E338", {"start": v(0.08, 10.02) * mm, "end": v(0.35, 8.66) * mm});
            skLineSegment(sketch, "E339", {"start": v(0.35, 8.66) * mm, "end": v(0.6, 7.94) * mm});
            skLineSegment(sketch, "E340", {"start": v(0.6, 7.94) * mm, "end": v(1.14, 8.96) * mm});
            skLineSegment(sketch, "E341", {"start": v(1.14, 8.96) * mm, "end": v(1.92, 9.92) * mm});
            skLineSegment(sketch, "E342", {"start": v(1.92, 9.92) * mm, "end": v(3.02, 10.77) * mm});
            skLineSegment(sketch, "E343", {"start": v(3.02, 10.77) * mm, "end": v(3.9, 11.57) * mm});
            skLineSegment(sketch, "E344", {"start": v(3.9, 11.57) * mm, "end": v(2.8, 10.29) * mm});
            skLineSegment(sketch, "E345", {"start": v(2.8, 10.29) * mm, "end": v(2.35, 9.62) * mm});
            skLineSegment(sketch, "E346", {"start": v(2.35, 9.62) * mm, "end": v(2.05, 8.86) * mm});
            skLineSegment(sketch, "E347", {"start": v(2.05, 8.86) * mm, "end": v(1.97, 8.1) * mm});
            skLineSegment(sketch, "E348", {"start": v(1.97, 8.1) * mm, "end": v(2.08, 7.26) * mm});
            skLineSegment(sketch, "E349", {"start": v(2.08, 7.26) * mm, "end": v(2.51, 6.19) * mm});
            skLineSegment(sketch, "E350", {"start": v(2.51, 6.19) * mm, "end": v(2.8, 5.4) * mm});
            skLineSegment(sketch, "E351", {"start": v(2.8, 5.4) * mm, "end": v(2.87, 4.79) * mm});
            skLineSegment(sketch, "E352", {"start": v(2.87, 4.79) * mm, "end": v(2.74, 4.12) * mm});
            skLineSegment(sketch, "E353", {"start": v(2.74, 4.12) * mm, "end": v(2.4, 3.28) * mm});
            skLineSegment(sketch, "E354", {"start": v(2.4, 3.28) * mm, "end": v(1.88, 2.8) * mm});
            skLineSegment(sketch, "E355", {"start": v(1.88, 2.8) * mm, "end": v(0.32, 2.02) * mm});
            skLineSegment(sketch, "E356", {"start": v(0.32, 2.02) * mm, "end": v(-1.15, 2.34) * mm});
            skLineSegment(sketch, "E357", {"start": v(-1.15, 2.34) * mm, "end": v(-2.25, 2.53) * mm});
            skLineSegment(sketch, "E358", {"start": v(-2.25, 2.53) * mm, "end": v(-2.87, 2.86) * mm});
            skLineSegment(sketch, "E359", {"start": v(-2.87, 2.86) * mm, "end": v(-3.32, 3.54) * mm});
            skLineSegment(sketch, "E360", {"start": v(-3.24, 3.3) * mm, "end": v(-3.32, 3.54) * mm});
            skLineSegment(sketch, "E361", {"start": v(-3.24, 3.3) * mm, "end": v(-3.24, 7.7) * mm});
            skLineSegment(sketch, "E362", {"start": v(-3.34, 7.33) * mm, "end": v(-3.24, 7.7) * mm});
            skLineSegment(sketch, "E363", {"start": v(-3.34, 7.33) * mm, "end": v(-3.17, 8.39) * mm});
            skLineSegment(sketch, "E364", {"start": v(-3.17, 8.39) * mm, "end": v(-3.15, 9.4) * mm});
            skLineSegment(sketch, "E365", {"start": v(-3.15, 9.4) * mm, "end": v(-3.24, 10.4) * mm});
            skLineSegment(sketch, "E366", {"start": v(-3.24, 10.4) * mm, "end": v(-2.6, 9.52) * mm});
            skLineSegment(sketch, "E367", {"start": v(-2.6, 9.52) * mm, "end": v(-2, 8.25) * mm});
            skLineSegment(sketch, "E368", {"start": v(-2, 8.25) * mm, "end": v(-1.45, 6.91) * mm});
            skLineSegment(sketch, "E369", {"start": v(-1.45, 6.91) * mm, "end": v(-1.14, 8.64) * mm});
            skLineSegment(sketch, "E370", {"start": v(-1.14, 8.64) * mm, "end": v(-0.65, 10.44) * mm});
            skLineSegment(sketch, "E371", {"start": v(-0.65, 10.44) * mm, "end": v(-0.12, 11.76) * mm});
            skLineSegment(sketch, "E372", {"start": v(-0.12, 11.76) * mm, "end": v(0.26, 12.17) * mm});
            skLineSegment(sketch, "E373", {"start": v(-0.2, 10.16) * mm, "end": v(-0.3, 8.76) * mm});
            skLineSegment(sketch, "E374", {"start": v(-0.3, 8.76) * mm, "end": v(-0.22, 7.77) * mm});
            skLineSegment(sketch, "E375", {"start": v(-0.22, 7.77) * mm, "end": v(0.03, 6.8) * mm});
            skLineSegment(sketch, "E376", {"start": v(0.03, 6.8) * mm, "end": v(0.48, 6.06) * mm});
            skLineSegment(sketch, "E377", {"start": v(0.48, 6.06) * mm, "end": v(0.96, 7.44) * mm});
            skLineSegment(sketch, "E378", {"start": v(0.96, 7.44) * mm, "end": v(1.42, 8.22) * mm});
            skLineSegment(sketch, "E379", {"start": v(1.42, 8.22) * mm, "end": v(1.69, 8.5) * mm});
            skLineSegment(sketch, "E380", {"start": v(1.69, 8.5) * mm, "end": v(1.49, 7.81) * mm});
            skLineSegment(sketch, "E381", {"start": v(1.49, 7.81) * mm, "end": v(1.49, 6.98) * mm});
            skLineSegment(sketch, "E382", {"start": v(1.49, 6.98) * mm, "end": v(1.64, 6.2) * mm});
            skLineSegment(sketch, "E383", {"start": v(1.64, 6.2) * mm, "end": v(1.89, 5.3) * mm});
            skLineSegment(sketch, "E384", {"start": v(1.89, 5.3) * mm, "end": v(2.15, 4.48) * mm});
            skLineSegment(sketch, "E385", {"start": v(2.15, 4.48) * mm, "end": v(2.2, 3.86) * mm});
            skLineSegment(sketch, "E386", {"start": v(2.2, 3.86) * mm, "end": v(2.1, 3.24) * mm});
            skLineSegment(sketch, "E387", {"start": v(2.1, 3.24) * mm, "end": v(1.69, 2.76) * mm});
            skLineSegment(sketch, "E388", {"start": v(1.69, 2.76) * mm, "end": v(0.32, 2) * mm});
            skLineSegment(sketch, "E389", {"start": v(0.32, 2) * mm, "end": v(-1.35, 2.46) * mm});
            skLineSegment(sketch, "E390", {"start": v(-1.35, 2.46) * mm, "end": v(-2.28, 2.98) * mm});
            skLineSegment(sketch, "E391", {"start": v(-2.28, 2.98) * mm, "end": v(-2.95, 3.88) * mm});
            skLineSegment(sketch, "E392", {"start": v(-2.95, 3.88) * mm, "end": v(-3.09, 4.55) * mm});
            skLineSegment(sketch, "E393", {"start": v(-3.09, 4.55) * mm, "end": v(-2.88, 5.3) * mm});
            skLineSegment(sketch, "E394", {"start": v(-2.88, 5.3) * mm, "end": v(-2.59, 6.3) * mm});
            skLineSegment(sketch, "E395", {"start": v(-2.59, 6.3) * mm, "end": v(-2.52, 7.23) * mm});
            skLineSegment(sketch, "E396", {"start": v(-2.52, 7.23) * mm, "end": v(-2.57, 7.85) * mm});
            skLineSegment(sketch, "E397", {"start": v(-2.57, 7.85) * mm, "end": v(-2.1, 6.91) * mm});
            skLineSegment(sketch, "E398", {"start": v(-2.1, 6.91) * mm, "end": v(-1.58, 5.68) * mm});
            skLineSegment(sketch, "E399", {"start": v(-1.58, 5.68) * mm, "end": v(-1.35, 5.22) * mm});
            skLineSegment(sketch, "E400", {"start": v(-1.35, 5.22) * mm, "end": v(-1.1, 6.55) * mm});
            skLineSegment(sketch, "E401", {"start": v(-1.1, 6.55) * mm, "end": v(-0.71, 8.39) * mm});
            skLineSegment(sketch, "E402", {"start": v(-0.71, 8.39) * mm, "end": v(-0.5, 9.2) * mm});
            skLineSegment(sketch, "E403", {"start": v(-0.5, 9.2) * mm, "end": v(-0.2, 10.16) * mm});
            skLineSegment(sketch, "E404", {"start": v(-0.43, 7.2) * mm, "end": v(-0.46, 6.87) * mm});
            skLineSegment(sketch, "E405", {"start": v(-0.46, 6.87) * mm, "end": v(-0.42, 6.37) * mm});
            skLineSegment(sketch, "E406", {"start": v(-0.42, 6.37) * mm, "end": v(-0.22, 5.62) * mm});
            skLineSegment(sketch, "E407", {"start": v(-0.22, 5.62) * mm, "end": v(0.35, 4.48) * mm});
            skLineSegment(sketch, "E408", {"start": v(0.35, 4.48) * mm, "end": v(0.61, 5.44) * mm});
            skLineSegment(sketch, "E409", {"start": v(0.61, 5.44) * mm, "end": v(0.85, 5.89) * mm});
            skLineSegment(sketch, "E410", {"start": v(0.85, 5.89) * mm, "end": v(1.2, 6.25) * mm});
            skLineSegment(sketch, "E411", {"start": v(1.2, 6.25) * mm, "end": v(1.08, 5.93) * mm});
            skLineSegment(sketch, "E412", {"start": v(1.08, 5.93) * mm, "end": v(1.05, 5.5) * mm});
            skLineSegment(sketch, "E413", {"start": v(1.05, 5.5) * mm, "end": v(1.16, 4.94) * mm});
            skLineSegment(sketch, "E414", {"start": v(1.16, 4.94) * mm, "end": v(1.4, 4.3) * mm});
            skLineSegment(sketch, "E415", {"start": v(1.4, 4.3) * mm, "end": v(1.6, 3.8) * mm});
            skLineSegment(sketch, "E416", {"start": v(1.6, 3.8) * mm, "end": v(1.73, 3.53) * mm});
            skLineSegment(sketch, "E417", {"start": v(1.73, 3.53) * mm, "end": v(1.62, 3.26) * mm});
            skLineSegment(sketch, "E418", {"start": v(1.62, 3.26) * mm, "end": v(1.1, 2.54) * mm});
            skLineSegment(sketch, "E419", {"start": v(1.1, 2.54) * mm, "end": v(0.32, 2.15) * mm});
            skLineSegment(sketch, "E420", {"start": v(0.32, 2.15) * mm, "end": v(-1.36, 2.71) * mm});
            skLineSegment(sketch, "E421", {"start": v(-1.36, 2.71) * mm, "end": v(-1.98, 3.13) * mm});
            skLineSegment(sketch, "E422", {"start": v(-1.98, 3.13) * mm, "end": v(-2.3, 3.61) * mm});
            skLineSegment(sketch, "E423", {"start": v(-2.3, 3.61) * mm, "end": v(-2.46, 4.24) * mm});
            skLineSegment(sketch, "E424", {"start": v(-2.46, 4.24) * mm, "end": v(-2.35, 4.93) * mm});
            skLineSegment(sketch, "E425", {"start": v(-2.35, 4.93) * mm, "end": v(-2.2, 5.68) * mm});
            skLineSegment(sketch, "E426", {"start": v(-2.2, 5.68) * mm, "end": v(-2.2, 6.23) * mm});
            skLineSegment(sketch, "E427", {"start": v(-2.2, 6.23) * mm, "end": v(-1.9, 5.63) * mm});
            skLineSegment(sketch, "E428", {"start": v(-1.9, 5.63) * mm, "end": v(-1.53, 5.12) * mm});
            skLineSegment(sketch, "E429", {"start": v(-1.53, 5.12) * mm, "end": v(-0.94, 4.43) * mm});
            skLineSegment(sketch, "E430", {"start": v(-0.94, 4.43) * mm, "end": v(-0.88, 5.45) * mm});
            skLineSegment(sketch, "E431", {"start": v(-0.88, 5.45) * mm, "end": v(-0.76, 6.29) * mm});
            skLineSegment(sketch, "E432", {"start": v(-0.76, 6.29) * mm, "end": v(-0.57, 6.95) * mm});
            skLineSegment(sketch, "E433", {"start": v(-0.57, 6.95) * mm, "end": v(-0.43, 7.2) * mm});
            skLineSegment(sketch, "E434", {"start": v(1.01, 4.55) * mm, "end": v(0.99, 4.14) * mm});
            skLineSegment(sketch, "E435", {"start": v(0.99, 4.14) * mm, "end": v(1.11, 3.5) * mm});
            skLineSegment(sketch, "E436", {"start": v(1.11, 3.5) * mm, "end": v(1.24, 3.03) * mm});
            skLineSegment(sketch, "E437", {"start": v(1.24, 3.03) * mm, "end": v(1.17, 2.64) * mm});
            skLineSegment(sketch, "E438", {"start": v(1.17, 2.64) * mm, "end": v(0.32, 2.22) * mm});
            skLineSegment(sketch, "E439", {"start": v(0.32, 2.22) * mm, "end": v(-0.76, 2.6) * mm});
            skLineSegment(sketch, "E440", {"start": v(-0.76, 2.6) * mm, "end": v(-1.42, 2.95) * mm});
            skLineSegment(sketch, "E441", {"start": v(-1.42, 2.95) * mm, "end": v(-1.75, 3.25) * mm});
            skLineSegment(sketch, "E442", {"start": v(-1.75, 3.25) * mm, "end": v(-1.89, 3.52) * mm});
            skLineSegment(sketch, "E443", {"start": v(-1.89, 3.52) * mm, "end": v(-1.92, 4.08) * mm});
            skLineSegment(sketch, "E444", {"start": v(-1.92, 4.08) * mm, "end": v(-1.92, 4.62) * mm});
            skLineSegment(sketch, "E445", {"start": v(-1.92, 4.62) * mm, "end": v(-2.1, 5.08) * mm});
            skLineSegment(sketch, "E446", {"start": v(-2.1, 5.08) * mm, "end": v(-1.66, 4.57) * mm});
            skLineSegment(sketch, "E447", {"start": v(-1.66, 4.57) * mm, "end": v(-0.78, 3.68) * mm});
            skLineSegment(sketch, "E448", {"start": v(-0.78, 3.68) * mm, "end": v(-0.5, 3.47) * mm});
            skLineSegment(sketch, "E449", {"start": v(-0.5, 3.47) * mm, "end": v(-0.46, 4.13) * mm});
            skLineSegment(sketch, "E450", {"start": v(-0.46, 4.13) * mm, "end": v(-0.33, 4.63) * mm});
            skLineSegment(sketch, "E451", {"start": v(-0.33, 4.63) * mm, "end": v(-0.2, 4.03) * mm});
            skLineSegment(sketch, "E452", {"start": v(-0.2, 4.03) * mm, "end": v(0.02, 3.58) * mm});
            skLineSegment(sketch, "E453", {"start": v(0.02, 3.58) * mm, "end": v(0.4, 3.04) * mm});
            skLineSegment(sketch, "E454", {"start": v(0.4, 3.04) * mm, "end": v(0.45, 3.8) * mm});
            skLineSegment(sketch, "E455", {"start": v(0.45, 3.8) * mm, "end": v(0.62, 4.23) * mm});
            skLineSegment(sketch, "E456", {"start": v(0.62, 4.23) * mm, "end": v(1.01, 4.55) * mm});
            skSolve(sketch);
        }
        {
            var Q0;
            Q0=makeQuery(id+"F8.imprint","IMPRINT",FACE,{"disambiguationData":[TD([[makeQuery(id+"F8.imprint","IMPRINT",EDGE,{"derivedFrom":sQuery(id+"F8.wireOp",EDGE,"E373")}),-1.0]])]});
            extrude(context, id + "F9", {"entities" : qUnion([Q0]), "operationType" : NewBodyOperationType.ADD, "depth" : 5.08 * mm, "offsetDistance" : 25.4 * mm});
        }
        {
            var Q0;
            Q0=makeQuery(id+"F9.opExtrude","CAP_FACE",FACE,{"disambiguationData":[OSD([sQuery(id+"F8.wireOp",EDGE,"E355"),sQuery(id+"F8.wireOp",EDGE,"E356"),sQuery(id+"F8.wireOp",EDGE,"E373"),sQuery(id+"F8.wireOp",EDGE,"E374"),sQuery(id+"F8.wireOp",EDGE,"E375"),sQuery(id+"F8.wireOp",EDGE,"E376"),sQuery(id+"F8.wireOp",EDGE,"E377"),sQuery(id+"F8.wireOp",EDGE,"E378"),sQuery(id+"F8.wireOp",EDGE,"E379"),sQuery(id+"F8.wireOp",EDGE,"E380"),sQuery(id+"F8.wireOp",EDGE,"E381"),sQuery(id+"F8.wireOp",EDGE,"E382"),sQuery(id+"F8.wireOp",EDGE,"E383"),sQuery(id+"F8.wireOp",EDGE,"E384"),sQuery(id+"F8.wireOp",EDGE,"E385"),sQuery(id+"F8.wireOp",EDGE,"E386"),sQuery(id+"F8.wireOp",EDGE,"E387"),sQuery(id+"F8.wireOp",EDGE,"E388"),sQuery(id+"F8.wireOp",EDGE,"E389"),sQuery(id+"F8.wireOp",EDGE,"E390"),sQuery(id+"F8.wireOp",EDGE,"E391"),sQuery(id+"F8.wireOp",EDGE,"E392"),sQuery(id+"F8.wireOp",EDGE,"E393"),sQuery(id+"F8.wireOp",EDGE,"E394"),sQuery(id+"F8.wireOp",EDGE,"E395"),sQuery(id+"F8.wireOp",EDGE,"E396"),sQuery(id+"F8.wireOp",EDGE,"E397"),sQuery(id+"F8.wireOp",EDGE,"E398"),sQuery(id+"F8.wireOp",EDGE,"E399"),sQuery(id+"F8.wireOp",EDGE,"E400"),sQuery(id+"F8.wireOp",EDGE,"E401"),sQuery(id+"F8.wireOp",EDGE,"E402"),sQuery(id+"F8.wireOp",EDGE,"E403"),sQuery(id+"F8.wireOp",EDGE,"E404"),sQuery(id+"F8.wireOp",EDGE,"E405"),sQuery(id+"F8.wireOp",EDGE,"E406"),sQuery(id+"F8.wireOp",EDGE,"E407"),sQuery(id+"F8.wireOp",EDGE,"E408"),sQuery(id+"F8.wireOp",EDGE,"E409"),sQuery(id+"F8.wireOp",EDGE,"E410"),sQuery(id+"F8.wireOp",EDGE,"E411"),sQuery(id+"F8.wireOp",EDGE,"E412"),sQuery(id+"F8.wireOp",EDGE,"E413"),sQuery(id+"F8.wireOp",EDGE,"E414"),sQuery(id+"F8.wireOp",EDGE,"E415"),sQuery(id+"F8.wireOp",EDGE,"E416"),sQuery(id+"F8.wireOp",EDGE,"E417"),sQuery(id+"F8.wireOp",EDGE,"E418"),sQuery(id+"F8.wireOp",EDGE,"E419"),sQuery(id+"F8.wireOp",EDGE,"E420"),sQuery(id+"F8.wireOp",EDGE,"E421"),sQuery(id+"F8.wireOp",EDGE,"E422"),sQuery(id+"F8.wireOp",EDGE,"E423"),sQuery(id+"F8.wireOp",EDGE,"E424"),sQuery(id+"F8.wireOp",EDGE,"E425"),sQuery(id+"F8.wireOp",EDGE,"E426"),sQuery(id+"F8.wireOp",EDGE,"E427"),sQuery(id+"F8.wireOp",EDGE,"E428"),sQuery(id+"F8.wireOp",EDGE,"E429"),sQuery(id+"F8.wireOp",EDGE,"E430"),sQuery(id+"F8.wireOp",EDGE,"E431"),sQuery(id+"F8.wireOp",EDGE,"E432"),sQuery(id+"F8.wireOp",EDGE,"E433")])],"isStart":false});
            extrude(context, id + "F10", {"entities" : qUnion([Q0]), "operationType" : NewBodyOperationType.ADD, "oppositeDirection" : true, "depth" : 10.16 * mm, "offsetDistance" : 25.4 * mm});
        }
    });
